AUTODESK INVENTOR PART (.ipt)
format: ipt  version: 2021 (Build 250183000, 183)  size: 257,536 bytes
history: native  units: mm
features: extrude x9, sketch x6, fillet x6, projected_geometry x3, chamfer x1, plane x1
ambient origin geometry x8: Origin, YZ Plane, XZ Plane, XY Plane, X Axis, Y Axis, Z Axis, Center Point
bodies: Solid1 (feature_tree)
feature tree (26):
  extrude  "Extrusion1"  Depth=8.2mm
  sketch  "Sketch2"  dims[d3=8.0mm d4=16.0mm]
  extrude  "Extrusion2"  Depth=16.0mm
  extrude  "Extrusion3"  Depth=8.2mm
  fillet  "Fillet1"  Radius=4.0mm
  extrude  "Extrusion4"  Depth=8.2mm
  fillet  "Fillet3"  Radius=16.0mm
  fillet  "Fillet4"  Radius=16.0mm
  extrude  "Extrusion7"  TaperAngle=0.0deg  [1 undecoded]
  extrude  "Extrusion5"  Depth=4.1mm
  extrude  "Extrusion6"  Depth=8.2mm
  fillet  "Fillet5"  Radius=4.1mm
  fillet  "Fillet6"  Radius=4.1mm
  extrude  "Extrusion8"  TaperAngle=0.0deg  [1 undecoded]
  chamfer  "Chamfer1"  Distance=4.1mm
  fillet  "Fillet7"  Radius=4.1mm
  plane  "Work Plane1"
  extrude  "Extrusion9"  Depth=4.1mm
  sketch  "Sketch1"  dims[d1=100.0mm d2=8.2mm]
  projected_geometry  "Projected Loop1"
  sketch  "Sketch3"  dims[d5=16.0mm d6=8.2mm d7=4.0mm d8=0.0mm]
  projected_geometry  "Projected Loop2"
  sketch  "Sketch5"  dims[d9=8.2mm d10=8.2mm d11=16.0mm d12=16.0mm]
  sketch  "Sketch7"  dims[d13=4.2mm d14=0.0mm]
  projected_geometry  "Projected Loop3"
  sketch  "Sketch8"  dims[d15=14.0mm d16=0.0mm d18=4.1mm d19=8.2mm d20=4.1mm d21=4.1mm d22=0.0mm d23=0.0mm d25=4.1mm d26=4.1mm d29=8.0mm d32=4.2mm d33=0.0mm d34=3.5mm d35=4.1mm d37=3.5mm d39=0.0mm d40=0.0mm d41=4.1mm d42=2.0mm d43=0.0mm d44=0.0mm d45=4.1mm d46=4.1mm d47=2.0mm d48=0.0mm d49=4.0mm d50=2.0mm d51=45.0deg d52=4.1mm d53=2.9mm d54=8.0mm d55=0.0mm d56=0.0mm d57=2.0mm d59=2.0mm d60=2.0mm d61=3.5mm d62=14.0mm]
note: 2 required parameter values undecoded (feature->parameter linkage not recoverable at this tier; creation-order binding heuristic only, values carry confidence <= 0.55)
